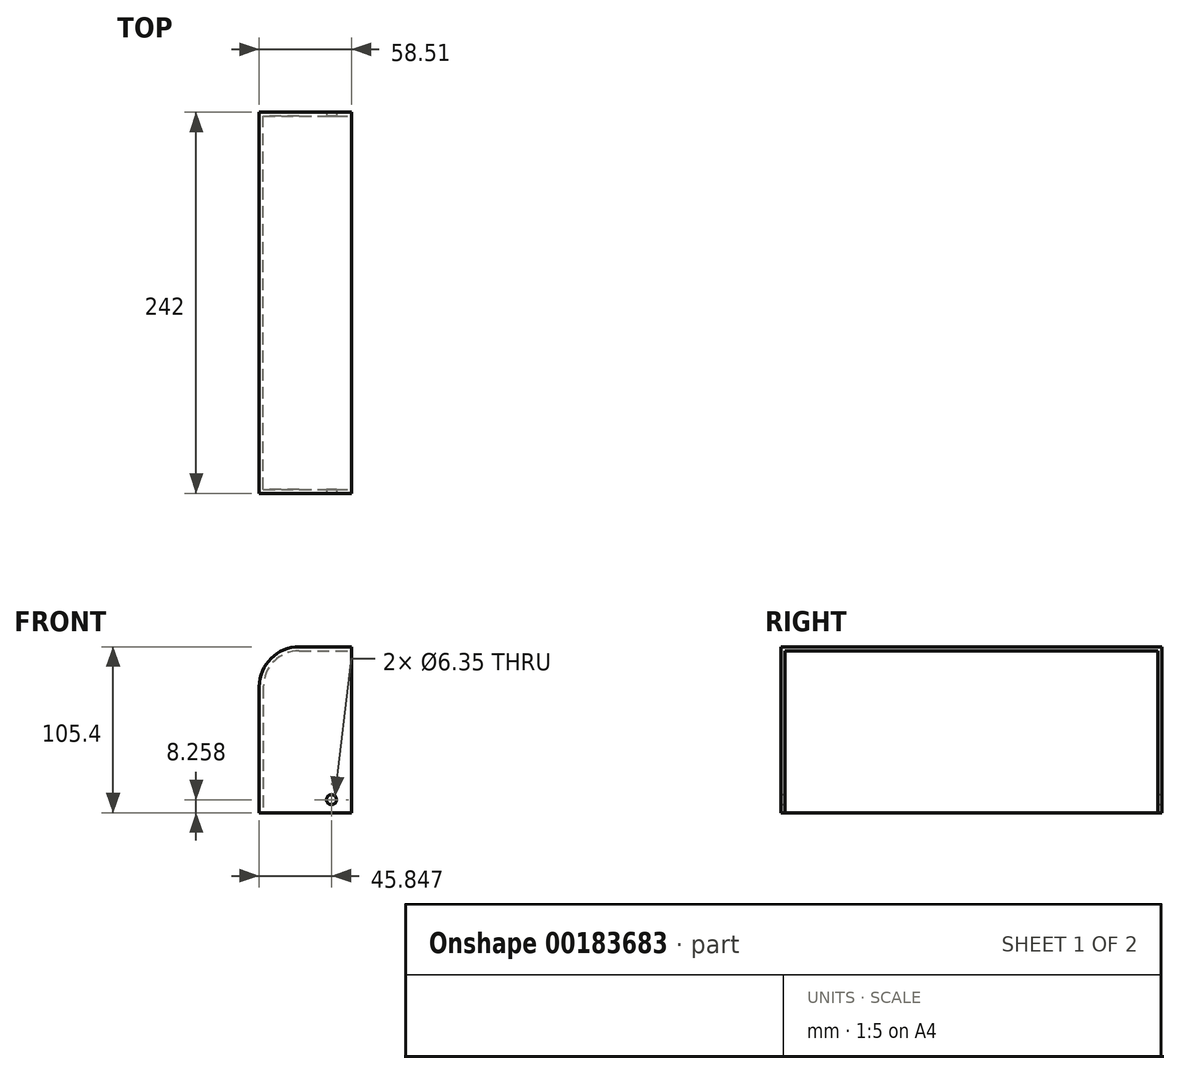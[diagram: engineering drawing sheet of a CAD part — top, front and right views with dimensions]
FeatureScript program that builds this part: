
annotation { "Feature Type Name" : "Feature", "Feature Type Description" : "" }
export const myFeature = defineFeature(function(context is Context, id is Id, definition is map)
    precondition{}
    {
        {
            var Q0;
            Q0=qCreatedBy(makeId("Front.planeOp"),FACE);
            var sketch = newSketch(context, id + "F0", { "sketchPlane" : qUnion([Q0])});
            skLineSegment(sketch, "E0.bottom", {"start": v(-2.65, 60.82) * mm, "end": v(30.46, 60.82) * mm});
            skLineSegment(sketch, "E0.top", {"start": v(-28.05, -44.58) * mm, "end": v(30.46, -44.58) * mm});
            skLineSegment(sketch, "E0.left", {"start": v(-28.05, 35.42) * mm, "end": v(-28.05, -44.58) * mm});
            skLineSegment(sketch, "E0.right", {"start": v(30.46, 60.82) * mm, "end": v(30.46, -44.58) * mm});
            skPoint(sketch, "E1.visualSharp", {"position": v(-28.05, 60.82) * mm});
            skArc(sketch, "E1.filletArc", {"start": v(-2.65, 60.82) * mm, "mid": v(-20.6, 53.38) * mm, "end": v(-28.05, 35.42) * mm});
            skSolve(sketch);
        }
        {
            var Q0;
            Q0=makeQuery(id+"F0.imprint","IMPRINT",FACE,{"disambiguationData":[TD([[makeQuery(id+"F0.imprint","IMPRINT",EDGE,{"derivedFrom":sQuery(id+"F0.wireOp",EDGE,"E0.bottom")}),-1.0]])]});
            extrude(context, id + "F1", {"entities" : qUnion([Q0]), "endBound" : BoundingType.SYMMETRIC, "depth" : 242 * mm});
        }
        {
            var Q0;
            Q0=makeQuery(id+"F1.opExtrude","SWEPT_FACE",FACE,{"disambiguationData":[OSD([sQuery(id+"F0.wireOp",EDGE,"E0.right")])]});
            var Q1;
            Q1=makeQuery(id+"F1.opExtrude","SWEPT_FACE",FACE,{"disambiguationData":[OSD([sQuery(id+"F0.wireOp",EDGE,"E0.top")])]});
            shell(context, id + "F2", {"entities" : qUnion([Q0, Q1]), "thickness" : 2.54 * mm});
        }
        {
            var Q0;
            Q0=makeQuery(id+"F1.opExtrude","CAP_FACE",FACE,{"disambiguationData":[OSD([sQuery(id+"F0.wireOp",EDGE,"E0.bottom"),sQuery(id+"F0.wireOp",EDGE,"E0.top"),sQuery(id+"F0.wireOp",EDGE,"E0.left"),sQuery(id+"F0.wireOp",EDGE,"E0.right"),sQuery(id+"F0.wireOp",EDGE,"E1.filletArc")])],"isStart":false});
            var sketch = newSketch(context, id + "F3", { "sketchPlane" : qUnion([Q0])});
            skCircle(sketch, "E2", {"center": v(17.8, -36.32) * mm, "radius": 4.48 * mm});
            skSolve(sketch);
        }
        {
            var Q0;
            Q0=sQuery(id+"F3.wireOp",VERTEX,"E2.center");
            var Q1;
            Q1=makeQuery(id+"F1.opExtrude","SWEPT_BODY",BODY,{"disambiguationData":[OSD([sQuery(id+"F0.wireOp",EDGE,"E0.bottom"),sQuery(id+"F0.wireOp",EDGE,"E0.top"),sQuery(id+"F0.wireOp",EDGE,"E0.left"),sQuery(id+"F0.wireOp",EDGE,"E0.right"),sQuery(id+"F0.wireOp",EDGE,"E1.filletArc")])]});
            hole(context, id + "F4", {"style" : HoleStyle.SIMPLE, "endStyle" : HoleEndStyle.THROUGH, "holeDiameter" : 6.35 * mm, "locations" : qUnion([Q0]), "scope" : qUnion([Q1]), "isTappedThrough" : true});
        }
    });
